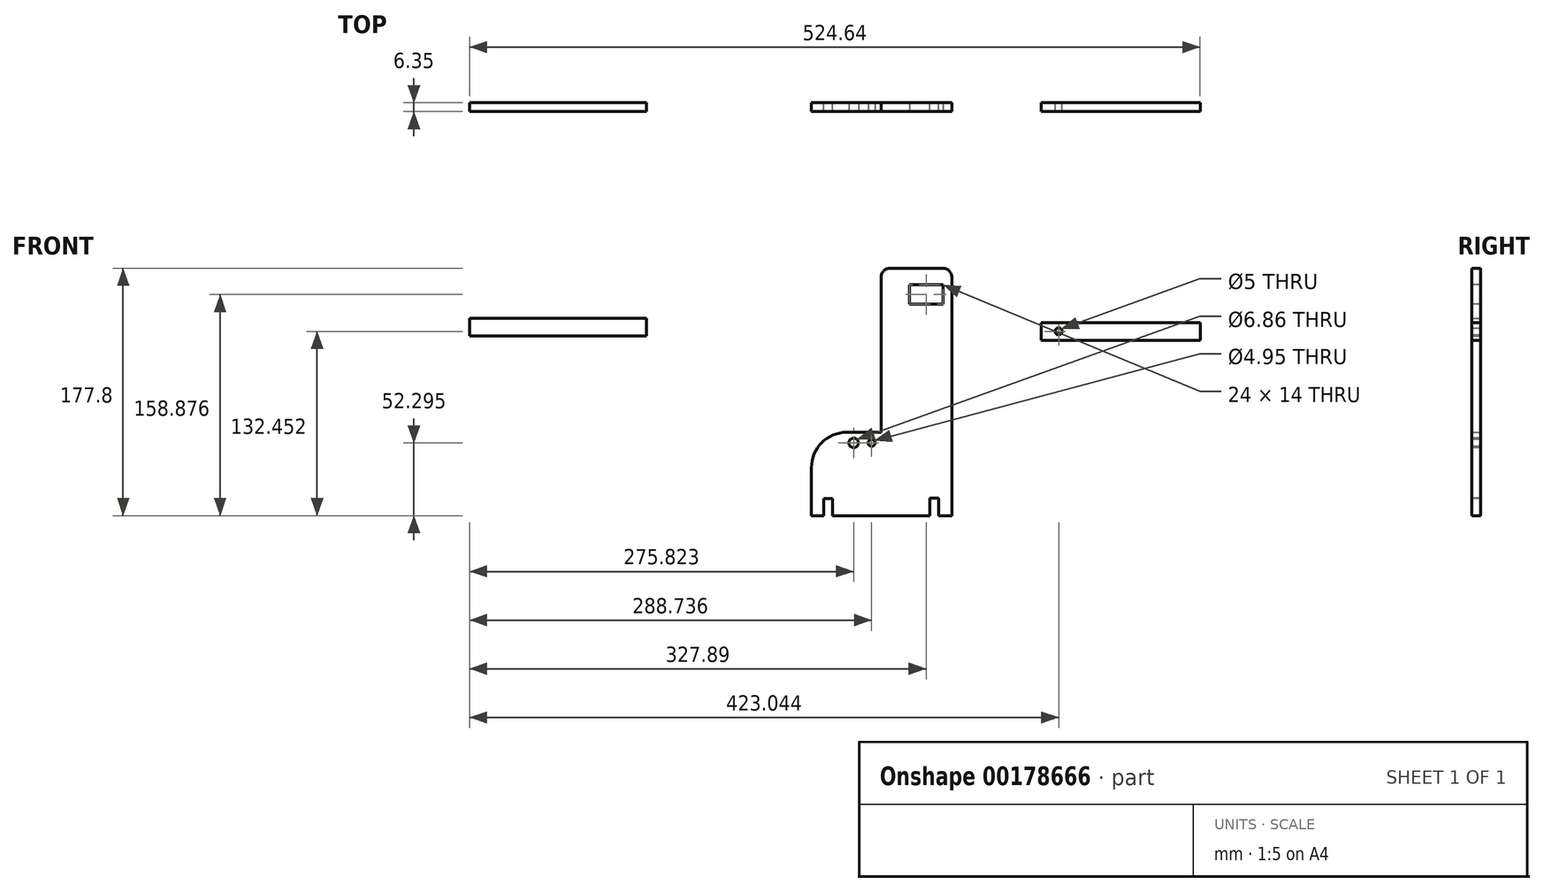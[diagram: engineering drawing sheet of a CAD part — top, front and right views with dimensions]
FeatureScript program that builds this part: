
annotation { "Feature Type Name" : "Feature", "Feature Type Description" : "" }
export const myFeature = defineFeature(function(context is Context, id is Id, definition is map)
    precondition{}
    {
        {
            var Q0;
            Q0=qCreatedBy(makeId("Front.planeOp"),FACE);
            var sketch = newSketch(context, id + "F0", { "sketchPlane" : qUnion([Q0])});
            skLineSegment(sketch, "E0.bottom", {"start": v(-38, 64.19) * mm, "end": v(0.1, 64.19) * mm});
            skLineSegment(sketch, "E0.top", {"start": v(-44.34, -113.61) * mm, "end": v(6.46, -113.61) * mm});
            skLineSegment(sketch, "E0.left", {"start": v(-44.34, 57.84) * mm, "end": v(-44.34, -113.61) * mm});
            skLineSegment(sketch, "E0.right", {"start": v(6.46, 57.84) * mm, "end": v(6.46, -113.61) * mm});
            skLineSegment(sketch, "E1.bottom", {"start": v(-44.34, -113.61) * mm, "end": v(-94.44, -113.61) * mm});
            skLineSegment(sketch, "E1.top", {"start": v(-44.34, -53.67) * mm, "end": v(-69.04, -53.67) * mm});
            skLineSegment(sketch, "E1.left", {"start": v(-44.34, -113.61) * mm, "end": v(-44.34, -53.67) * mm});
            skLineSegment(sketch, "E1.right", {"start": v(-94.44, -113.61) * mm, "end": v(-94.44, -79.07) * mm});
            skPoint(sketch, "E2.visualSharp", {"position": v(-94.44, -53.67) * mm});
            skArc(sketch, "E2.filletArc", {"start": v(-69.04, -53.67) * mm, "mid": v(-87, -61.11) * mm, "end": v(-94.44, -79.07) * mm});
            skPoint(sketch, "E3.visualSharp", {"position": v(-44.34, 64.19) * mm});
            skArc(sketch, "E3.filletArc", {"start": v(-38, 64.19) * mm, "mid": v(-42.48, 62.33) * mm, "end": v(-44.34, 57.84) * mm});
            skPoint(sketch, "E4.visualSharp", {"position": v(6.46, 64.19) * mm});
            skArc(sketch, "E4.filletArc", {"start": v(6.46, 57.84) * mm, "mid": v(4.6, 62.33) * mm, "end": v(0.1, 64.19) * mm});
            skLineSegment(sketch, "E5.bottom", {"start": v(2.72, -113.61) * mm, "end": v(-3.53, -113.61) * mm});
            skLineSegment(sketch, "E5.top", {"start": v(2.72, -100.91) * mm, "end": v(-3.53, -100.91) * mm});
            skLineSegment(sketch, "E5.left", {"start": v(2.72, -113.61) * mm, "end": v(2.72, -100.91) * mm});
            skLineSegment(sketch, "E5.right", {"start": v(-3.53, -113.61) * mm, "end": v(-3.53, -100.91) * mm});
            skLineSegment(sketch, "E6.bottom", {"start": v(-83, -113.61) * mm, "end": v(-89.25, -113.61) * mm});
            skLineSegment(sketch, "E6.top", {"start": v(-83, -100.91) * mm, "end": v(-89.25, -100.91) * mm});
            skLineSegment(sketch, "E6.left", {"start": v(-83, -113.61) * mm, "end": v(-83, -100.91) * mm});
            skLineSegment(sketch, "E6.right", {"start": v(-89.25, -113.61) * mm, "end": v(-89.25, -100.91) * mm});
            skSolve(sketch);
        }
        {
            var Q0;
            Q0 = qSketchRegion(id + "F0", true);
            extrude(context, id + "F1", {"entities" : qUnion([Q0]), "depth" : 6.35 * mm});
        }
        {
            var Q0;
            Q0=qCreatedBy(makeId("Front.planeOp"),FACE);
            var sketch = newSketch(context, id + "F2", { "sketchPlane" : qUnion([Q0])});
            skLineSegment(sketch, "E7.bottom", {"start": v(70.45, 25.2) * mm, "end": v(184.75, 25.2) * mm});
            skLineSegment(sketch, "E7.top", {"start": v(70.45, 12.5) * mm, "end": v(184.75, 12.5) * mm});
            skLineSegment(sketch, "E7.left", {"start": v(70.45, 25.2) * mm, "end": v(70.45, 12.5) * mm});
            skLineSegment(sketch, "E7.right", {"start": v(184.75, 25.2) * mm, "end": v(184.75, 12.5) * mm});
            skCircle(sketch, "E8", {"center": v(83.15, 18.84) * mm, "radius": 2.5 * mm});
            skLineSegment(sketch, "E9.bottom", {"start": v(180.8, 25.2) * mm, "end": v(180.16, 25.2) * mm});
            skLineSegment(sketch, "E9.top", {"start": v(180.8, 24.56) * mm, "end": v(180.16, 24.56) * mm});
            skLineSegment(sketch, "E9.left", {"start": v(180.8, 25.2) * mm, "end": v(180.8, 24.56) * mm});
            skLineSegment(sketch, "E9.right", {"start": v(180.16, 25.2) * mm, "end": v(180.16, 24.56) * mm});
            skLineSegment(sketch, "E10.bottom", {"start": v(174.29, 25.2) * mm, "end": v(174.92, 25.2) * mm});
            skLineSegment(sketch, "E10.top", {"start": v(174.29, 24.56) * mm, "end": v(174.92, 24.56) * mm});
            skLineSegment(sketch, "E10.left", {"start": v(174.29, 25.2) * mm, "end": v(174.29, 24.56) * mm});
            skLineSegment(sketch, "E10.right", {"start": v(174.92, 25.2) * mm, "end": v(174.92, 24.56) * mm});
            skSolve(sketch);
        }
        {
            var Q0;
            Q0 = qSketchRegion(id + "F2", true);
            extrude(context, id + "F3", {"entities" : qUnion([Q0]), "depth" : 6.35 * mm});
        }
        {
            var Q0;
            Q0=makeQuery(id+"F1.opExtrude","CAP_FACE",FACE,{"disambiguationData":[OSD([sQuery(id+"F0.wireOp",EDGE,"E0.bottom"),sQuery(id+"F0.wireOp",EDGE,"E0.top"),sQuery(id+"F0.wireOp",EDGE,"E0.left"),sQuery(id+"F0.wireOp",EDGE,"E0.right"),sQuery(id+"F0.wireOp",EDGE,"E1.bottom"),sQuery(id+"F0.wireOp",EDGE,"E1.top"),sQuery(id+"F0.wireOp",EDGE,"E1.right"),sQuery(id+"F0.wireOp",EDGE,"E2.filletArc"),sQuery(id+"F0.wireOp",EDGE,"E3.filletArc"),sQuery(id+"F0.wireOp",EDGE,"E4.filletArc"),sQuery(id+"F0.wireOp",EDGE,"E5.bottom"),sQuery(id+"F0.wireOp",EDGE,"E6.bottom")])],"isStart":false});
            var sketch = newSketch(context, id + "F4", { "sketchPlane" : qUnion([Q0])});
            skSolve(sketch);
        }
        {
            var Q0;
            Q0=makeQuery(id+"F4.imprint","IMPRINT",FACE,{"disambiguationData":[TD([[makeQuery(id+"F4.imprint","IMPRINT",EDGE,{"derivedFrom":makeQuery(id+"F1.opExtrude","CAP_EDGE",EDGE,{"disambiguationData":[OSD([sQuery(id+"F0.wireOp",EDGE,"E0.bottom")])],"isStart":false})}),-1.0]])]});
            var sketch = newSketch(context, id + "F5", { "sketchPlane" : qUnion([Q0])});
            skLineSegment(sketch, "E11.bottom", {"start": v(-85.53, -113.93) * mm, "end": v(-79.18, -113.93) * mm});
            skLineSegment(sketch, "E11.top", {"start": v(-85.53, -101.23) * mm, "end": v(-79.18, -101.23) * mm});
            skLineSegment(sketch, "E11.left", {"start": v(-85.53, -113.93) * mm, "end": v(-85.53, -101.23) * mm});
            skLineSegment(sketch, "E11.right", {"start": v(-79.18, -113.93) * mm, "end": v(-79.18, -101.23) * mm});
            skLineSegment(sketch, "E12.bottom", {"start": v(-9.48, -113.7) * mm, "end": v(-3.13, -113.7) * mm});
            skLineSegment(sketch, "E12.top", {"start": v(-9.48, -101) * mm, "end": v(-3.13, -101) * mm});
            skLineSegment(sketch, "E12.left", {"start": v(-9.48, -113.7) * mm, "end": v(-9.48, -101) * mm});
            skLineSegment(sketch, "E12.right", {"start": v(-3.13, -113.7) * mm, "end": v(-3.13, -101) * mm});
            skSolve(sketch);
        }
        {
            var Q0;
            Q0 = qSketchRegion(id + "F5", true);
            extrude(context, id + "F6", {"entities" : qUnion([Q0]), "operationType" : NewBodyOperationType.REMOVE, "oppositeDirection" : true, "depth" : 18.8 * mm});
        }
        {
            var Q0;
            Q0=qCreatedBy(makeId("Front.planeOp"),FACE);
            var sketch = newSketch(context, id + "F7", { "sketchPlane" : qUnion([Q0])});
            skLineSegment(sketch, "E13.bottom", {"start": v(-339.89, 28.33) * mm, "end": v(-212.89, 28.33) * mm});
            skLineSegment(sketch, "E13.top", {"start": v(-339.89, 15.63) * mm, "end": v(-212.89, 15.63) * mm});
            skLineSegment(sketch, "E13.left", {"start": v(-339.89, 28.33) * mm, "end": v(-339.89, 15.63) * mm});
            skLineSegment(sketch, "E13.right", {"start": v(-212.89, 28.33) * mm, "end": v(-212.89, 15.63) * mm});
            skSolve(sketch);
        }
        {
            var Q0;
            Q0 = qSketchRegion(id + "F7", true);
            extrude(context, id + "F8", {"entities" : qUnion([Q0]), "depth" : 6.35 * mm});
        }
        {
            var Q0;
            Q0=makeQuery(id+"F4.imprint","IMPRINT",FACE,{"disambiguationData":[TD([[makeQuery(id+"F4.imprint","IMPRINT",EDGE,{"derivedFrom":makeQuery(id+"F1.opExtrude","CAP_EDGE",EDGE,{"disambiguationData":[OSD([sQuery(id+"F0.wireOp",EDGE,"E0.bottom")])],"isStart":false})}),-1.0]])]});
            var sketch = newSketch(context, id + "F9", { "sketchPlane" : qUnion([Q0])});
            skCircle(sketch, "E14", {"center": v(-51.15, -61.31) * mm, "radius": 2.48 * mm});
            skCircle(sketch, "E15", {"center": v(-64.07, -61.31) * mm, "radius": 3.43 * mm});
            skSolve(sketch);
        }
        {
            var Q0;
            Q0 = qSketchRegion(id + "F9", true);
            extrude(context, id + "F10", {"entities" : qUnion([Q0]), "operationType" : NewBodyOperationType.REMOVE, "oppositeDirection" : true, "depth" : 10.67 * mm});
        }
        {
            var Q0;
            Q0=makeQuery(id+"F4.imprint","IMPRINT",FACE,{"disambiguationData":[TD([[makeQuery(id+"F4.imprint","IMPRINT",EDGE,{"derivedFrom":makeQuery(id+"F1.opExtrude","CAP_EDGE",EDGE,{"disambiguationData":[OSD([sQuery(id+"F0.wireOp",EDGE,"E0.bottom")])],"isStart":false})}),-1.0]])]});
            var sketch = newSketch(context, id + "F11", { "sketchPlane" : qUnion([Q0])});
            skLineSegment(sketch, "E16.bottom", {"start": v(-24, 52.27) * mm, "end": v(0, 52.27) * mm});
            skLineSegment(sketch, "E16.top", {"start": v(-24, 38.27) * mm, "end": v(0, 38.27) * mm});
            skLineSegment(sketch, "E16.left", {"start": v(-24, 52.27) * mm, "end": v(-24, 38.27) * mm});
            skLineSegment(sketch, "E16.right", {"start": v(0, 52.27) * mm, "end": v(0, 38.27) * mm});
            skSolve(sketch);
        }
        {
            var Q0;
            Q0 = qSketchRegion(id + "F11", true);
            extrude(context, id + "F12", {"entities" : qUnion([Q0]), "operationType" : NewBodyOperationType.REMOVE, "oppositeDirection" : true, "depth" : 12.6 * mm});
        }
    });
